FCSTD DOCUMENT  (FreeCAD 0.21R33771 (Git))
Label: drift1_dipole
License: All rights reserved
LicenseURL: https://en.wikipedia.org/wiki/All_rights_reserved
objects: Sketcher::SketchObject×2, Part::Sweep×1
note: 3 computed .brp shape members not serialized (recipe doc carries the construction recipe); baked Part::Feature solids carry a one-line shape summary decoded from their .brp

FEATURE [Sketcher::SketchObject] Sketch
  FullyConstrained = true
  Placement = pos=(0,0,0) rot=(1,0,0;1.5708rad)
  expr: Constraints[9] = 5000 mm
  sketch-geometry (5):
    g0: ArcOfCircle CenterX=-500002 CenterY=5000 CenterZ=0 NormalX=0 NormalY=0 NormalZ=1 AngleXU=0 Radius=500002 StartAngle=0 EndAngle=0.01
    g1: LineSegment StartX=-500002 StartY=5000 StartZ=0 EndX=0 EndY=5000 EndZ=0
    g2: LineSegment StartX=-500002 StartY=5000 StartZ=0 EndX=-24.9999 EndY=9999.94 EndZ=0
    g3: LineSegment StartX=0 StartY=0 StartZ=0 EndX=0 EndY=5000 EndZ=0
    g4: LineSegment StartX=-24.9999 StartY=9999.94 StartZ=0 EndX=-124.998 EndY=19999.4 EndZ=0
  constraints (14):
    c: Coincident(g1,g0)
    c: Coincident(g1,g0)
    c: Horizontal(g1)
    c: Coincident(g2,g0)
    c: Coincident(g2,g0)
    c: Angle(g1,g2) = 0.01
    c: DistanceX(g1,g1) = 500002
    c: Coincident(g3,g-1)
    c: PointOnObject(g3,g-2)
    c: DistanceY(g3,g3) = 5000
    c: Coincident(g0,g3)
    c: Coincident(g4,g0)
    c: Distance(g4) = 10000
    c: Angle(g3,g4) = 0.01
FEATURE [Sketcher::SketchObject] Sketch001
  FullyConstrained = true
  sketch-geometry (5):
    g0: LineSegment StartX=-25 StartY=-25 StartZ=0 EndX=-25 EndY=25 EndZ=0
    g1: LineSegment StartX=-25 StartY=25 StartZ=0 EndX=25 EndY=25 EndZ=0
    g2: LineSegment StartX=25 StartY=25 StartZ=0 EndX=25 EndY=-25 EndZ=0
    g3: LineSegment StartX=25 StartY=-25 StartZ=0 EndX=-25 EndY=-25 EndZ=0
    g4: GeomPoint X=3e-15 Y=0 Z=0
  constraints (12):
    c: Coincident(g0,g1)
    c: Coincident(g1,g2)
    c: Coincident(g2,g3)
    c: Coincident(g3,g0)
    c: Horizontal(g1)
    c: Horizontal(g3)
    c: Vertical(g0)
    c: Vertical(g2)
    c: Symmetric(g1,g0,g4)
    c: Coincident(g4,g-1)
    c: DistanceY(g2,g2) = 50
    c: DistanceX(g1,g1) = 50
FEATURE [Part::Sweep] Sweep
  Frenet = false
  Sections = -> [Sketch001]
  Solid = true
  Spine = -> Sketch [Edge1,Edge2,Edge3]
  Transition = 1
